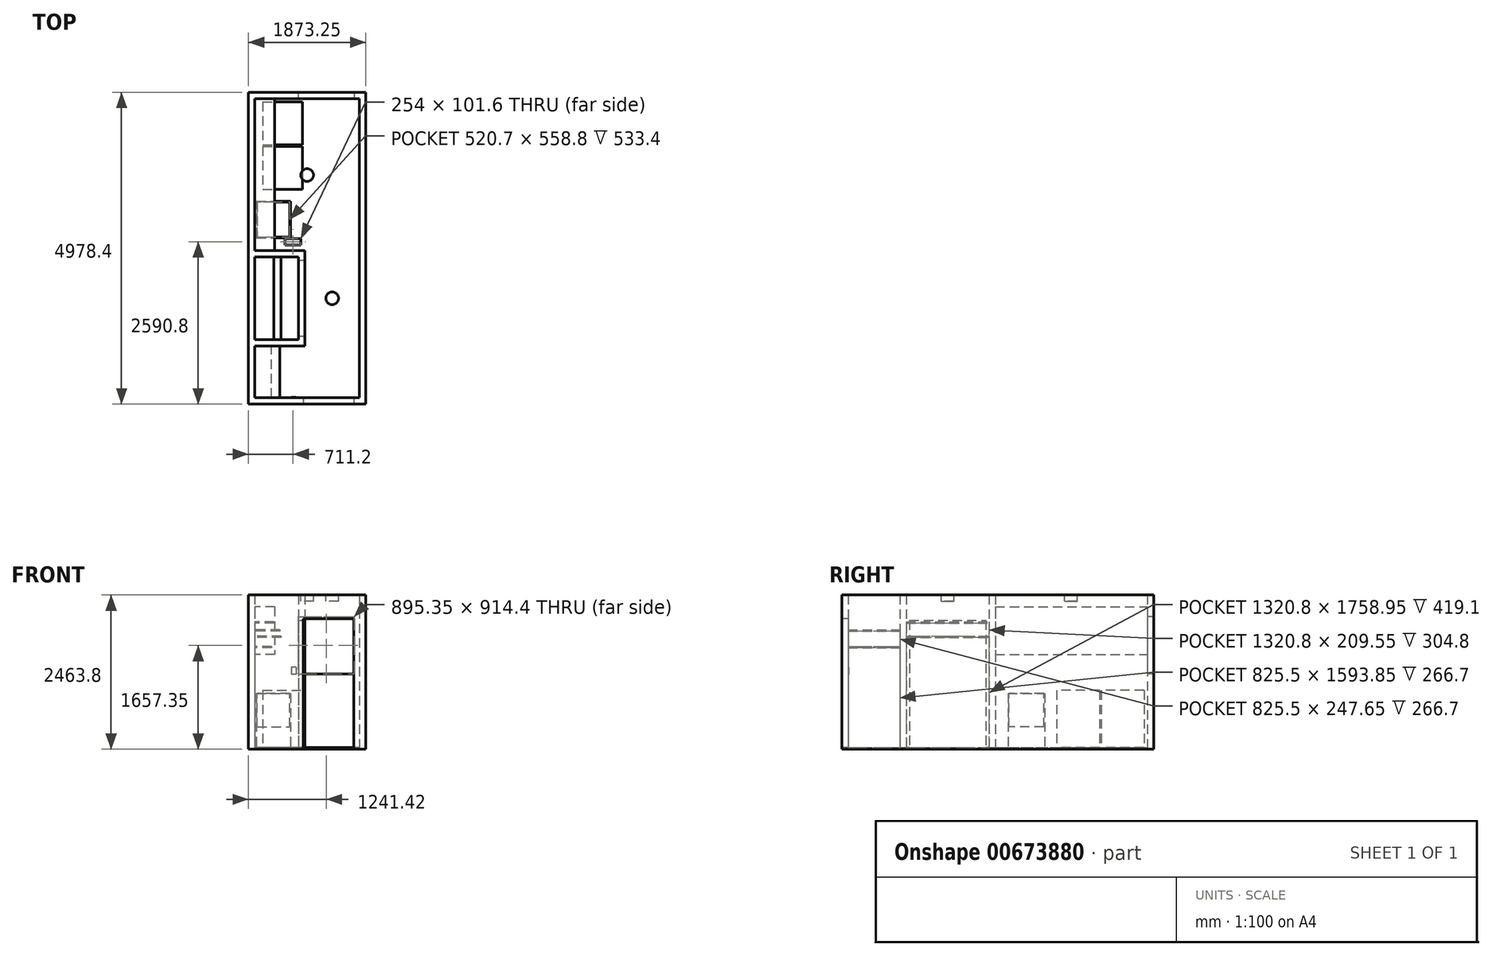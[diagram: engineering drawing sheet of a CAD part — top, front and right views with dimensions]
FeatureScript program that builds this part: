
annotation { "Feature Type Name" : "Feature", "Feature Type Description" : "" }
export const myFeature = defineFeature(function(context is Context, id is Id, definition is map)
    precondition{}
    {
        {
            var Q0;
            Q0=qCreatedBy(makeId("Top.planeOp"),FACE);
            var sketch = newSketch(context, id + "F0", { "sketchPlane" : qUnion([Q0])});
            skLineSegment(sketch, "E0.bottom", {"start": v(0, 0) * mm, "end": v(-1670.05, 0) * mm});
            skLineSegment(sketch, "E0.top", {"start": v(0, 4775.2) * mm, "end": v(-1670.05, 4775.2) * mm});
            skLineSegment(sketch, "E0.left", {"start": v(0, 0) * mm, "end": v(0, 4775.2) * mm});
            skLineSegment(sketch, "E0.right", {"start": v(-1670.05, 0) * mm, "end": v(-1670.05, 4775.2) * mm});
            skLineSegment(sketch, "E1.0", {"start": v(-1771.65, -101.6) * mm, "end": v(-1771.65, 4876.8) * mm});
            skLineSegment(sketch, "E1.1", {"start": v(101.6, -101.6) * mm, "end": v(-1771.65, -101.6) * mm});
            skLineSegment(sketch, "E1.2", {"start": v(101.6, -101.6) * mm, "end": v(101.6, 4876.8) * mm});
            skLineSegment(sketch, "E1.3", {"start": v(101.6, 4876.8) * mm, "end": v(-1771.65, 4876.8) * mm});
            skSolve(sketch);
        }
        {
            var Q0;
            Q0 = qSketchRegion(id + "F0", true);
            extrude(context, id + "F1", {"entities" : qUnion([Q0]), "depth" : 2438.4 * mm, "offsetDistance" : 25.4 * mm});
        }
        {
            var Q0;
            Q0=makeQuery(id+"F1.opExtrude","SWEPT_FACE",FACE,{"disambiguationData":[OSD([sQuery(id+"F0.wireOp",EDGE,"E1.1")])]});
            var sketch = newSketch(context, id + "F2", { "sketchPlane" : qUnion([Q0])});
            skLineSegment(sketch, "E2.bottom", {"start": v(-88.9, 0) * mm, "end": v(-895.35, 0) * mm});
            skLineSegment(sketch, "E2.top", {"start": v(-88.9, 2057.4) * mm, "end": v(-895.35, 2057.4) * mm});
            skLineSegment(sketch, "E2.left", {"start": v(-88.9, 0) * mm, "end": v(-88.9, 2057.4) * mm});
            skLineSegment(sketch, "E2.right", {"start": v(-895.35, 0) * mm, "end": v(-895.35, 2057.4) * mm});
            skSolve(sketch);
        }
        {
            var Q0;
            Q0 = qSketchRegion(id + "F2", true);
            extrude(context, id + "F3", {"entities" : qUnion([Q0]), "operationType" : NewBodyOperationType.REMOVE, "endBound" : BoundingType.UP_TO_NEXT, "oppositeDirection" : true, "depth" : 25.4 * mm, "offsetDistance" : 25.4 * mm});
        }
        {
            var Q0;
            Q0=makeQuery(id+"F1.opExtrude","SWEPT_FACE",FACE,{"disambiguationData":[OSD([sQuery(id+"F0.wireOp",EDGE,"E0.top")])]});
            var sketch = newSketch(context, id + "F4", { "sketchPlane" : qUnion([Q0])});
            skLineSegment(sketch, "E3.bottom", {"start": v(-977.9, 2089.15) * mm, "end": v(-82.55, 2089.15) * mm});
            skLineSegment(sketch, "E3.top", {"start": v(-977.9, 1174.75) * mm, "end": v(-82.55, 1174.75) * mm});
            skLineSegment(sketch, "E3.left", {"start": v(-977.9, 2089.15) * mm, "end": v(-977.9, 1174.75) * mm});
            skLineSegment(sketch, "E3.right", {"start": v(-82.55, 2089.15) * mm, "end": v(-82.55, 1174.75) * mm});
            skSolve(sketch);
        }
        {
            var Q0;
            Q0 = qSketchRegion(id + "F4", true);
            extrude(context, id + "F5", {"entities" : qUnion([Q0]), "operationType" : NewBodyOperationType.REMOVE, "endBound" : BoundingType.UP_TO_NEXT, "oppositeDirection" : true, "depth" : 25.4 * mm, "offsetDistance" : 25.4 * mm});
        }
        {
            var Q0;
            Q0=makeQuery(id+"F1.opExtrude","CAP_FACE",FACE,{"disambiguationData":[OSD([sQuery(id+"F0.wireOp",EDGE,"E0.bottom"),sQuery(id+"F0.wireOp",EDGE,"E0.top"),sQuery(id+"F0.wireOp",EDGE,"E0.left"),sQuery(id+"F0.wireOp",EDGE,"E0.right"),sQuery(id+"F0.wireOp",EDGE,"E1.0"),sQuery(id+"F0.wireOp",EDGE,"E1.1"),sQuery(id+"F0.wireOp",EDGE,"E1.2"),sQuery(id+"F0.wireOp",EDGE,"E1.3")])],"isStart":true});
            var sketch = newSketch(context, id + "F6", { "sketchPlane" : qUnion([Q0])});
            skLineSegment(sketch, "E4.bottom", {"start": v(101.6, 101.6) * mm, "end": v(-1771.65, 101.6) * mm});
            skLineSegment(sketch, "E4.top", {"start": v(101.6, -4876.8) * mm, "end": v(-1771.65, -4876.8) * mm});
            skLineSegment(sketch, "E4.left", {"start": v(101.6, 101.6) * mm, "end": v(101.6, -4876.8) * mm});
            skLineSegment(sketch, "E4.right", {"start": v(-1771.65, 101.6) * mm, "end": v(-1771.65, -4876.8) * mm});
            skLineSegment(sketch, "E5.bottom", {"start": v(-1187.45, -2438.4) * mm, "end": v(-933.45, -2438.4) * mm});
            skLineSegment(sketch, "E5.top", {"start": v(-1187.45, -2540) * mm, "end": v(-933.45, -2540) * mm});
            skLineSegment(sketch, "E5.left", {"start": v(-1187.45, -2438.4) * mm, "end": v(-1187.45, -2540) * mm});
            skLineSegment(sketch, "E5.right", {"start": v(-933.45, -2438.4) * mm, "end": v(-933.45, -2540) * mm});
            skSolve(sketch);
        }
        {
            var Q0;
            Q0 = qSketchRegion(id + "F6", true);
            extrude(context, id + "F7", {"entities" : qUnion([Q0]), "operationType" : NewBodyOperationType.ADD, "depth" : 25.4 * mm, "offsetDistance" : 25.4 * mm});
        }
        {
            var Q0;
            Q0=makeQuery(id+"F7.opExtrude","CAP_FACE",FACE,{"disambiguationData":[OSD([sQuery(id+"F6.wireOp",EDGE,"E4.bottom"),sQuery(id+"F6.wireOp",EDGE,"E4.top"),sQuery(id+"F6.wireOp",EDGE,"E4.left"),sQuery(id+"F6.wireOp",EDGE,"E4.right")])],"isStart":true});
            var sketch = newSketch(context, id + "F8", { "sketchPlane" : qUnion([Q0])});
            skLineSegment(sketch, "E6", {"start": v(-1670.05, 825.5) * mm, "end": v(-869.95, 825.5) * mm});
            skLineSegment(sketch, "E7", {"start": v(-869.95, 825.5) * mm, "end": v(-869.95, 977.9) * mm});
            skLineSegment(sketch, "E8", {"start": v(-869.95, 977.9) * mm, "end": v(-971.55, 977.9) * mm});
            skLineSegment(sketch, "E9", {"start": v(-971.55, 977.9) * mm, "end": v(-971.55, 927.1) * mm});
            skLineSegment(sketch, "E10", {"start": v(-971.55, 927.1) * mm, "end": v(-1670.05, 927.1) * mm});
            skLineSegment(sketch, "E11", {"start": v(-1670.05, 927.1) * mm, "end": v(-1670.05, 825.5) * mm});
            skLineSegment(sketch, "E12", {"start": v(-1670.05, 2247.9) * mm, "end": v(-971.55, 2247.9) * mm});
            skLineSegment(sketch, "E13", {"start": v(-971.55, 2247.9) * mm, "end": v(-971.55, 2197.1) * mm});
            skLineSegment(sketch, "E14", {"start": v(-971.55, 2197.1) * mm, "end": v(-869.95, 2197.1) * mm});
            skLineSegment(sketch, "E15", {"start": v(-869.95, 2197.1) * mm, "end": v(-869.95, 2349.5) * mm});
            skLineSegment(sketch, "E16", {"start": v(-869.95, 2349.5) * mm, "end": v(-1670.05, 2349.5) * mm});
            skLineSegment(sketch, "E17", {"start": v(-1670.05, 2349.5) * mm, "end": v(-1670.05, 2247.9) * mm});
            skSolve(sketch);
        }
        {
            var Q0;
            Q0 = qSketchRegion(id + "F8", true);
            var Q1;
            Q1=makeQuery(id+"F1.opExtrude","CAP_FACE",FACE,{"disambiguationData":[OSD([sQuery(id+"F0.wireOp",EDGE,"E0.bottom"),sQuery(id+"F0.wireOp",EDGE,"E0.top"),sQuery(id+"F0.wireOp",EDGE,"E0.left"),sQuery(id+"F0.wireOp",EDGE,"E0.right"),sQuery(id+"F0.wireOp",EDGE,"E1.0"),sQuery(id+"F0.wireOp",EDGE,"E1.1"),sQuery(id+"F0.wireOp",EDGE,"E1.2"),sQuery(id+"F0.wireOp",EDGE,"E1.3")])],"isStart":false});
            extrude(context, id + "F9", {"entities" : qUnion([Q0]), "operationType" : NewBodyOperationType.ADD, "endBound" : BoundingType.UP_TO_SURFACE, "depth" : 25.4 * mm, "endBoundEntityFace" : qUnion([Q1]), "offsetDistance" : 25.4 * mm});
        }
        {
            var Q0;
            Q0=makeQuery(id+"F9.opExtrude","SWEPT_FACE",FACE,{"disambiguationData":[OSD([sQuery(id+"F8.wireOp",EDGE,"E7")])]});
            var sketch = newSketch(context, id + "F10", { "sketchPlane" : qUnion([Q0])});
            skLineSegment(sketch, "E18.0", {"start": v(2197.1, 2438.4) * mm, "end": v(2197.1, 0) * mm});
            skLineSegment(sketch, "E19.bottom", {"start": v(977.9, 2438.4) * mm, "end": v(2197.1, 2438.4) * mm});
            skLineSegment(sketch, "E19.top", {"start": v(977.9, 2032) * mm, "end": v(2197.1, 2032) * mm});
            skLineSegment(sketch, "E19.left", {"start": v(977.9, 2438.4) * mm, "end": v(977.9, 2032) * mm});
            skLineSegment(sketch, "E19.right", {"start": v(2197.1, 2438.4) * mm, "end": v(2197.1, 2032) * mm});
            skSolve(sketch);
        }
        {
            var Q0;
            Q0 = qSketchRegion(id + "F10", true);
            var Q1;
            Q1=makeQuery(id+"F9.opExtrude","SWEPT_FACE",FACE,{"disambiguationData":[OSD([sQuery(id+"F8.wireOp",EDGE,"E9")])]});
            extrude(context, id + "F11", {"entities" : qUnion([Q0]), "operationType" : NewBodyOperationType.ADD, "endBound" : BoundingType.UP_TO_SURFACE, "oppositeDirection" : true, "depth" : 25.4 * mm, "endBoundEntityFace" : qUnion([Q1]), "offsetDistance" : 25.4 * mm});
        }
        {
            var Q0;
            Q0=makeQuery(id+"F7.opExtrude","CAP_FACE",FACE,{"disambiguationData":[OSD([sQuery(id+"F6.wireOp",EDGE,"E4.bottom"),sQuery(id+"F6.wireOp",EDGE,"E4.top"),sQuery(id+"F6.wireOp",EDGE,"E4.left"),sQuery(id+"F6.wireOp",EDGE,"E4.right")])],"isStart":true});
            var sketch = newSketch(context, id + "F12", { "sketchPlane" : qUnion([Q0])});
            skLineSegment(sketch, "E20.bottom", {"start": v(-1543.05, 4724.4) * mm, "end": v(-908.05, 4724.4) * mm});
            skLineSegment(sketch, "E20.top", {"start": v(-1543.05, 4038.6) * mm, "end": v(-908.05, 4038.6) * mm});
            skLineSegment(sketch, "E20.left", {"start": v(-1543.05, 4724.4) * mm, "end": v(-1543.05, 4038.6) * mm});
            skLineSegment(sketch, "E20.right", {"start": v(-908.05, 4724.4) * mm, "end": v(-908.05, 4038.6) * mm});
            skLineSegment(sketch, "E21.bottom", {"start": v(-1543.05, 4013.2) * mm, "end": v(-908.05, 4013.2) * mm});
            skLineSegment(sketch, "E21.top", {"start": v(-1543.05, 3327.4) * mm, "end": v(-908.05, 3327.4) * mm});
            skLineSegment(sketch, "E21.left", {"start": v(-1543.05, 4013.2) * mm, "end": v(-1543.05, 3327.4) * mm});
            skLineSegment(sketch, "E21.right", {"start": v(-908.05, 4013.2) * mm, "end": v(-908.05, 3327.4) * mm});
            skSolve(sketch);
        }
        {
            var Q0;
            Q0 = qSketchRegion(id + "F12", true);
            extrude(context, id + "F13", {"entities" : qUnion([Q0]), "depth" : 914.4 * mm, "offsetDistance" : 25.4 * mm});
        }
        {
            var Q0;
            Q0=makeQuery(id+"F7.opExtrude","CAP_FACE",FACE,{"disambiguationData":[OSD([sQuery(id+"F6.wireOp",EDGE,"E4.bottom"),sQuery(id+"F6.wireOp",EDGE,"E4.top"),sQuery(id+"F6.wireOp",EDGE,"E4.left"),sQuery(id+"F6.wireOp",EDGE,"E4.right"),sQuery(id+"F6.wireOp",EDGE,"E5.bottom"),sQuery(id+"F6.wireOp",EDGE,"E5.top"),sQuery(id+"F6.wireOp",EDGE,"E5.left"),sQuery(id+"F6.wireOp",EDGE,"E5.right")])],"isStart":true});
            var sketch = newSketch(context, id + "F14", { "sketchPlane" : qUnion([Q0])});
            skLineSegment(sketch, "E22.bottom", {"start": v(-1644.65, 2552.7) * mm, "end": v(-1098.55, 2552.7) * mm});
            skLineSegment(sketch, "E22.top", {"start": v(-1644.65, 3136.9) * mm, "end": v(-1098.55, 3136.9) * mm});
            skLineSegment(sketch, "E22.left", {"start": v(-1644.65, 2552.7) * mm, "end": v(-1644.65, 3136.9) * mm});
            skLineSegment(sketch, "E22.right", {"start": v(-1098.55, 2552.7) * mm, "end": v(-1098.55, 3136.9) * mm});
            skSolve(sketch);
        }
        {
            var Q0;
            Q0 = qSketchRegion(id + "F14", true);
            extrude(context, id + "F15", {"entities" : qUnion([Q0]), "depth" : 863.6 * mm, "offsetDistance" : 25.4 * mm});
        }
        {
            var Q0;
            Q0=makeQuery(id+"F15.opExtrude","CAP_FACE",FACE,{"disambiguationData":[OSD([sQuery(id+"F14.wireOp",EDGE,"E22.bottom"),sQuery(id+"F14.wireOp",EDGE,"E22.top"),sQuery(id+"F14.wireOp",EDGE,"E22.left"),sQuery(id+"F14.wireOp",EDGE,"E22.right")])],"isStart":false});
            var sketch = newSketch(context, id + "F16", { "sketchPlane" : qUnion([Q0])});
            skLineSegment(sketch, "E23.0", {"start": v(-1631.95, 2565.4) * mm, "end": v(-1111.25, 2565.4) * mm});
            skLineSegment(sketch, "E23.1", {"start": v(-1631.95, 3124.2) * mm, "end": v(-1631.95, 2565.4) * mm});
            skLineSegment(sketch, "E23.2", {"start": v(-1111.25, 3124.2) * mm, "end": v(-1631.95, 3124.2) * mm});
            skLineSegment(sketch, "E23.3", {"start": v(-1111.25, 2565.4) * mm, "end": v(-1111.25, 3124.2) * mm});
            skSolve(sketch);
        }
        {
            var Q0;
            {var subQ0=sQuery(id+"F0.wireOp",EDGE,"E0.top");var subQ5=sQuery(id+"F0.wireOp",EDGE,"E0.right");Q0=makeQuery(id+"F9.boolean.opBoolean","SPLIT",FACE,{"disambiguationData":[TD([makeQuery(id+"F1.opExtrude","SWEPT_FACE",FACE,{"disambiguationData":[OSD([subQ0])]})])],"derivedFrom":makeQuery(id+"F1.opExtrude","SWEPT_FACE",FACE,{"disambiguationData":[OSD([subQ5])]})});}
            var sketch = newSketch(context, id + "F17", { "sketchPlane" : qUnion([Q0])});
            skLineSegment(sketch, "E24.bottom", {"start": v(2349.5, 2247.9) * mm, "end": v(4775.2, 2247.9) * mm});
            skLineSegment(sketch, "E24.top", {"start": v(2349.5, 1485.9) * mm, "end": v(4775.2, 1485.9) * mm});
            skLineSegment(sketch, "E24.left", {"start": v(2349.5, 2247.9) * mm, "end": v(2349.5, 1485.9) * mm});
            skLineSegment(sketch, "E24.right", {"start": v(4775.2, 2247.9) * mm, "end": v(4775.2, 1485.9) * mm});
            skSolve(sketch);
        }
        {
            var Q0;
            Q0 = qSketchRegion(id + "F17", true);
            extrude(context, id + "F18", {"entities" : qUnion([Q0]), "depth" : 317.5 * mm, "offsetDistance" : 25.4 * mm});
        }
        {
            var Q0;
            Q0 = qSketchRegion(id + "F16", true);
            extrude(context, id + "F19", {"entities" : qUnion([Q0]), "operationType" : NewBodyOperationType.REMOVE, "oppositeDirection" : true, "depth" : 533.4 * mm, "offsetDistance" : 25.4 * mm});
        }
        {
            var Q0;
            {var subQ4=sQuery(id+"F0.wireOp",EDGE,"E0.right");var subQ7=sQuery(id+"F0.wireOp",EDGE,"E0.bottom");Q0=makeQuery(id+"F9.boolean.opBoolean","SPLIT",FACE,{"disambiguationData":[TD([makeQuery(id+"F1.opExtrude","SWEPT_FACE",FACE,{"disambiguationData":[OSD([subQ7])]})])],"derivedFrom":makeQuery(id+"F1.opExtrude","SWEPT_FACE",FACE,{"disambiguationData":[OSD([subQ4])]})});}
            var sketch = newSketch(context, id + "F20", { "sketchPlane" : qUnion([Q0])});
            skLineSegment(sketch, "E25.bottom", {"start": v(0, 1879.6) * mm, "end": v(825.5, 1879.6) * mm});
            skLineSegment(sketch, "E25.top", {"start": v(0, 1860.55) * mm, "end": v(825.5, 1860.55) * mm});
            skLineSegment(sketch, "E25.left", {"start": v(0, 1879.6) * mm, "end": v(0, 1860.55) * mm});
            skLineSegment(sketch, "E25.right", {"start": v(825.5, 1879.6) * mm, "end": v(825.5, 1860.55) * mm});
            skSolve(sketch);
        }
        {
            var Q0;
            Q0 = qSketchRegion(id + "F20", true);
            extrude(context, id + "F21", {"entities" : qUnion([Q0]), "operationType" : NewBodyOperationType.ADD, "depth" : 400.05 * mm, "offsetDistance" : 25.4 * mm});
        }
        {
            var Q0;
            {var subQ0=sQuery(id+"F0.wireOp",EDGE,"E0.bottom");var subQ1=makeQuery(id+"F1.opExtrude","SWEPT_FACE",FACE,{"disambiguationData":[OSD([subQ0])]});var subQ8=sQuery(id+"F0.wireOp",EDGE,"E0.right");Q0=makeQuery(id+"F21.boolean.opBoolean","SPLIT",FACE,{"disambiguationData":[TD([makeQuery(id+"F21.opExtrude","SWEPT_FACE",FACE,{"disambiguationData":[OSD([sQuery(id+"F20.wireOp",EDGE,"E25.top")])]})])],"derivedFrom":makeQuery(id+"F9.boolean.opBoolean","SPLIT",FACE,{"disambiguationData":[TD([subQ1])],"derivedFrom":makeQuery(id+"F1.opExtrude","SWEPT_FACE",FACE,{"disambiguationData":[OSD([subQ8])]})})});}
            var sketch = newSketch(context, id + "F22", { "sketchPlane" : qUnion([Q0])});
            skLineSegment(sketch, "E26.bottom", {"start": v(0, 1593.85) * mm, "end": v(825.5, 1593.85) * mm});
            skLineSegment(sketch, "E26.top", {"start": v(0, 1612.9) * mm, "end": v(825.5, 1612.9) * mm});
            skLineSegment(sketch, "E26.left", {"start": v(0, 1612.9) * mm, "end": v(0, 1593.85) * mm});
            skLineSegment(sketch, "E26.right", {"start": v(825.5, 1612.9) * mm, "end": v(825.5, 1593.85) * mm});
            skSolve(sketch);
        }
        {
            var Q0;
            Q0 = qSketchRegion(id + "F22", true);
            extrude(context, id + "F23", {"entities" : qUnion([Q0]), "operationType" : NewBodyOperationType.ADD, "depth" : 266.7 * mm, "offsetDistance" : 25.4 * mm});
        }
        {
            var Q0;
            {var subQ4=sQuery(id+"F0.wireOp",EDGE,"E0.right");Q0=makeQuery(id+"F9.boolean.opBoolean","SPLIT",FACE,{"disambiguationData":[TD([makeQuery(id+"F9.opExtrude","SWEPT_FACE",FACE,{"disambiguationData":[OSD([sQuery(id+"F8.wireOp",EDGE,"E10")])]})])],"derivedFrom":makeQuery(id+"F1.opExtrude","SWEPT_FACE",FACE,{"disambiguationData":[OSD([subQ4])]})});}
            var sketch = newSketch(context, id + "F24", { "sketchPlane" : qUnion([Q0])});
            skLineSegment(sketch, "E27.bottom", {"start": v(927.1, 2006.6) * mm, "end": v(2247.9, 2006.6) * mm});
            skLineSegment(sketch, "E27.top", {"start": v(927.1, 1987.55) * mm, "end": v(2247.9, 1987.55) * mm});
            skLineSegment(sketch, "E27.left", {"start": v(927.1, 2006.6) * mm, "end": v(927.1, 1987.55) * mm});
            skLineSegment(sketch, "E27.right", {"start": v(2247.9, 2006.6) * mm, "end": v(2247.9, 1987.55) * mm});
            skSolve(sketch);
        }
        {
            var Q0;
            Q0 = qSketchRegion(id + "F24", true);
            extrude(context, id + "F25", {"entities" : qUnion([Q0]), "operationType" : NewBodyOperationType.ADD, "depth" : 304.8 * mm, "offsetDistance" : 25.4 * mm});
        }
        {
            var Q0;
            {var subQ2=makeQuery(id+"F9.opExtrude","SWEPT_FACE",FACE,{"disambiguationData":[OSD([sQuery(id+"F8.wireOp",EDGE,"E10")])]});var subQ7=sQuery(id+"F0.wireOp",EDGE,"E0.right");Q0=makeQuery(id+"F25.boolean.opBoolean","SPLIT",FACE,{"disambiguationData":[TD([makeQuery(id+"F25.opExtrude","SWEPT_FACE",FACE,{"disambiguationData":[OSD([sQuery(id+"F24.wireOp",EDGE,"E27.top")])]})])],"derivedFrom":makeQuery(id+"F9.boolean.opBoolean","SPLIT",FACE,{"disambiguationData":[TD([subQ2])],"derivedFrom":makeQuery(id+"F1.opExtrude","SWEPT_FACE",FACE,{"disambiguationData":[OSD([subQ7])]})})});}
            var sketch = newSketch(context, id + "F26", { "sketchPlane" : qUnion([Q0])});
            skLineSegment(sketch, "E28.bottom", {"start": v(927.1, 1778) * mm, "end": v(2247.9, 1778) * mm});
            skLineSegment(sketch, "E28.top", {"start": v(927.1, 1758.95) * mm, "end": v(2247.9, 1758.95) * mm});
            skLineSegment(sketch, "E28.left", {"start": v(927.1, 1778) * mm, "end": v(927.1, 1758.95) * mm});
            skLineSegment(sketch, "E28.right", {"start": v(2247.9, 1778) * mm, "end": v(2247.9, 1758.95) * mm});
            skSolve(sketch);
        }
        {
            var Q0;
            Q0 = qSketchRegion(id + "F26", true);
            extrude(context, id + "F27", {"entities" : qUnion([Q0]), "operationType" : NewBodyOperationType.ADD, "depth" : 419.1 * mm, "offsetDistance" : 25.4 * mm});
        }
        {
            var Q0;
            Q0=makeQuery(id+"F1.opExtrude","SWEPT_FACE",FACE,{"disambiguationData":[OSD([sQuery(id+"F0.wireOp",EDGE,"E0.bottom")])]});
            var sketch = newSketch(context, id + "F28", { "sketchPlane" : qUnion([Q0])});
            skLineSegment(sketch, "E29.bottom", {"start": v(1009.65, 1282.7) * mm, "end": v(1085.85, 1282.7) * mm});
            skLineSegment(sketch, "E29.top", {"start": v(1009.65, 1168.4) * mm, "end": v(1085.85, 1168.4) * mm});
            skLineSegment(sketch, "E29.left", {"start": v(1009.65, 1282.7) * mm, "end": v(1009.65, 1168.4) * mm});
            skLineSegment(sketch, "E29.right", {"start": v(1085.85, 1282.7) * mm, "end": v(1085.85, 1168.4) * mm});
            skSolve(sketch);
        }
        {
            var Q0;
            Q0 = qSketchRegion(id + "F28", true);
            extrude(context, id + "F29", {"entities" : qUnion([Q0]), "depth" : 6.35 * mm, "offsetDistance" : 25.4 * mm});
        }
        {
            var Q0;
            {var subQ0=sQuery(id+"F0.wireOp",EDGE,"E1.3");var subQ1=sQuery(id+"F0.wireOp",EDGE,"E1.2");var subQ2=sQuery(id+"F0.wireOp",EDGE,"E1.1");var subQ3=sQuery(id+"F0.wireOp",EDGE,"E1.0");var subQ4=sQuery(id+"F0.wireOp",EDGE,"E0.right");var subQ5=sQuery(id+"F0.wireOp",EDGE,"E0.left");var subQ6=sQuery(id+"F0.wireOp",EDGE,"E0.top");var subQ7=sQuery(id+"F0.wireOp",EDGE,"E0.bottom");Q0=makeQuery(id+"F11.boolean.opBoolean","MERGE",FACE,{"derivedFrom":[makeQuery(id+"F9.boolean.opBoolean","MERGE",FACE,{"derivedFrom":[makeQuery(id+"F1.opExtrude","CAP_FACE",FACE,{"disambiguationData":[OSD([subQ7,subQ6,subQ5,subQ4,subQ3,subQ2,subQ1,subQ0])],"isStart":false}),makeQuery(id+"F9.opExtrude","CAP_FACE",FACE,{"disambiguationData":[OSD([subQ7,subQ6,subQ5,subQ4,subQ3,subQ2,subQ1,subQ0]),OD(0.0)],"isStart":false}),makeQuery(id+"F9.opExtrude","CAP_FACE",FACE,{"disambiguationData":[OSD([subQ7,subQ6,subQ5,subQ4,subQ3,subQ2,subQ1,subQ0]),OD(1.0)],"isStart":false})]}),makeQuery(id+"F11.opExtrude","SWEPT_FACE",FACE,{"disambiguationData":[OSD([sQuery(id+"F10.wireOp",EDGE,"E19.bottom")])]})]});}
            var sketch = newSketch(context, id + "F30", { "sketchPlane" : qUnion([Q0])});
            skCircle(sketch, "E30", {"center": v(-835.03, 3556) * mm, "radius": 101.6 * mm});
            skCircle(sketch, "E31", {"center": v(-434.98, 1587.5) * mm, "radius": 101.6 * mm});
            skLineSegment(sketch, "E32", {"start": v(-1670.05, 3556) * mm, "end": v(-835.03, 3556) * mm, "construction": true});
            skLineSegment(sketch, "E33", {"start": v(0, 3556) * mm, "end": v(-835.03, 3556) * mm, "construction": true});
            skLineSegment(sketch, "E34", {"start": v(-869.95, 1587.5) * mm, "end": v(0, 1587.5) * mm, "construction": true});
            skSolve(sketch);
        }
        {
            var Q0;
            Q0 = qSketchRegion(id + "F30", true);
            extrude(context, id + "F31", {"entities" : qUnion([Q0]), "oppositeDirection" : true, "depth" : 101.6 * mm, "offsetDistance" : 25.4 * mm});
        }
    });
